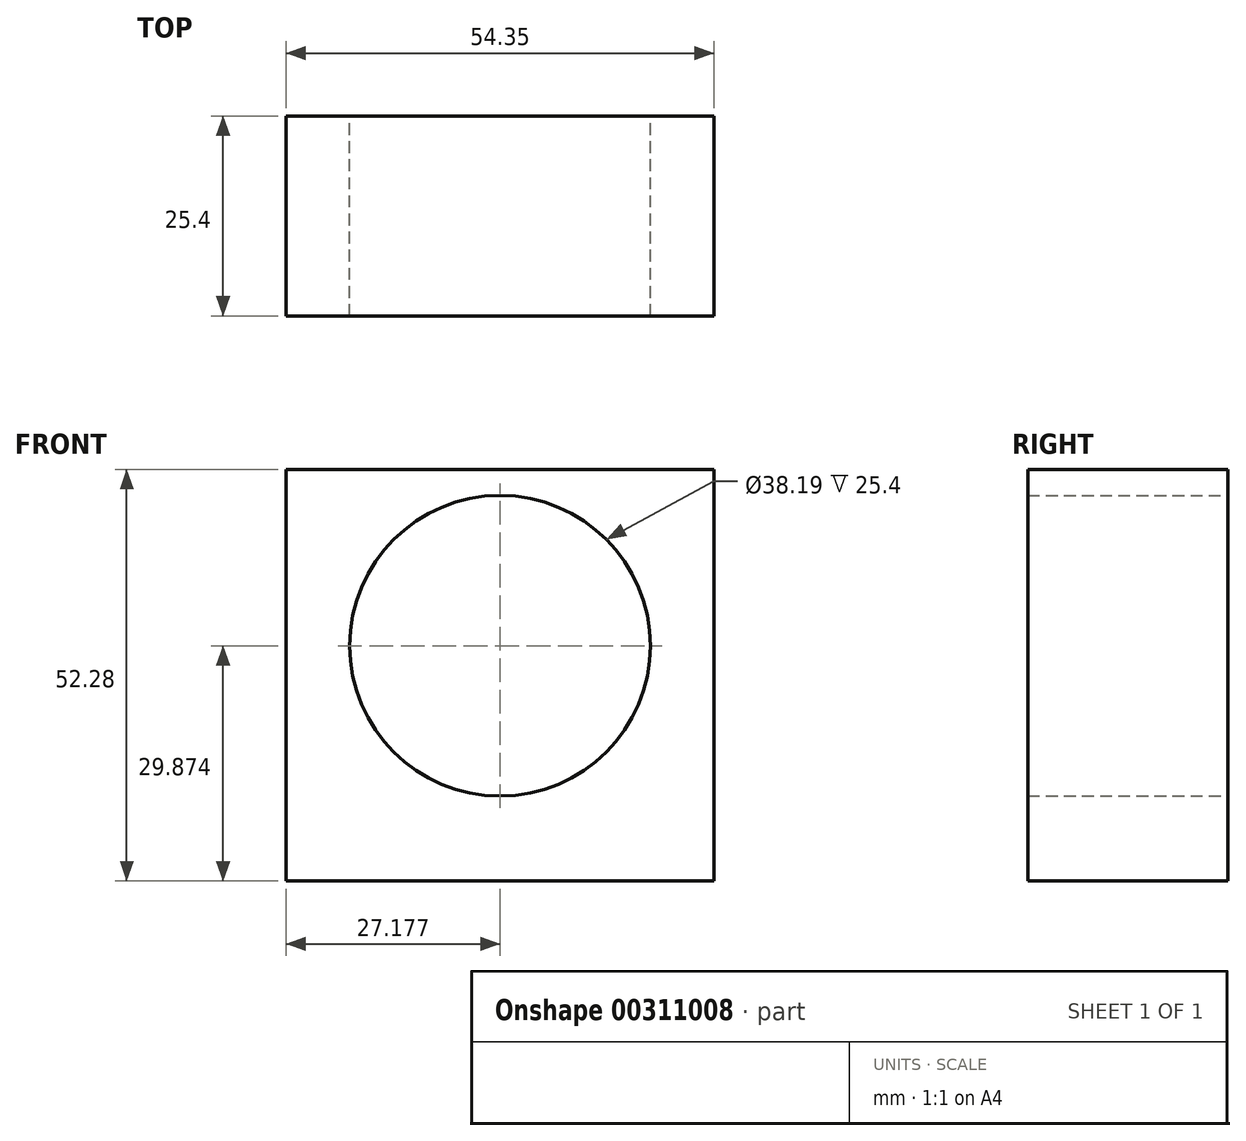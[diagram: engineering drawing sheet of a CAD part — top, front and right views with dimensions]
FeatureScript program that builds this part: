
annotation { "Feature Type Name" : "Feature", "Feature Type Description" : "" }
export const myFeature = defineFeature(function(context is Context, id is Id, definition is map)
    precondition{}
    {
        {
            var Q0;
            Q0=qCreatedBy(makeId("Front.planeOp"),FACE);
            var sketch = newSketch(context, id + "F0", { "sketchPlane" : qUnion([Q0])});
            skLineSegment(sketch, "E0.bottom", {"start": v(0, 0) * mm, "end": v(54.35, 0) * mm});
            skLineSegment(sketch, "E0.top", {"start": v(0, 52.28) * mm, "end": v(54.35, 52.28) * mm});
            skLineSegment(sketch, "E0.left", {"start": v(0, 0) * mm, "end": v(0, 52.28) * mm});
            skLineSegment(sketch, "E0.right", {"start": v(54.35, 0) * mm, "end": v(54.35, 52.28) * mm});
            skCircle(sketch, "E1", {"center": v(27.18, 29.87) * mm, "radius": 19.1 * mm});
            skPoint(sketch, "E1.centerSnap0", {"position": v(27.18, 52.28) * mm});
            skSolve(sketch);
        }
        {
            var Q0;
            Q0 = qSketchRegion(id + "F0", true);
            extrude(context, id + "F1", {"entities" : qUnion([Q0]), "depth" : 25.4 * mm});
        }
    });
